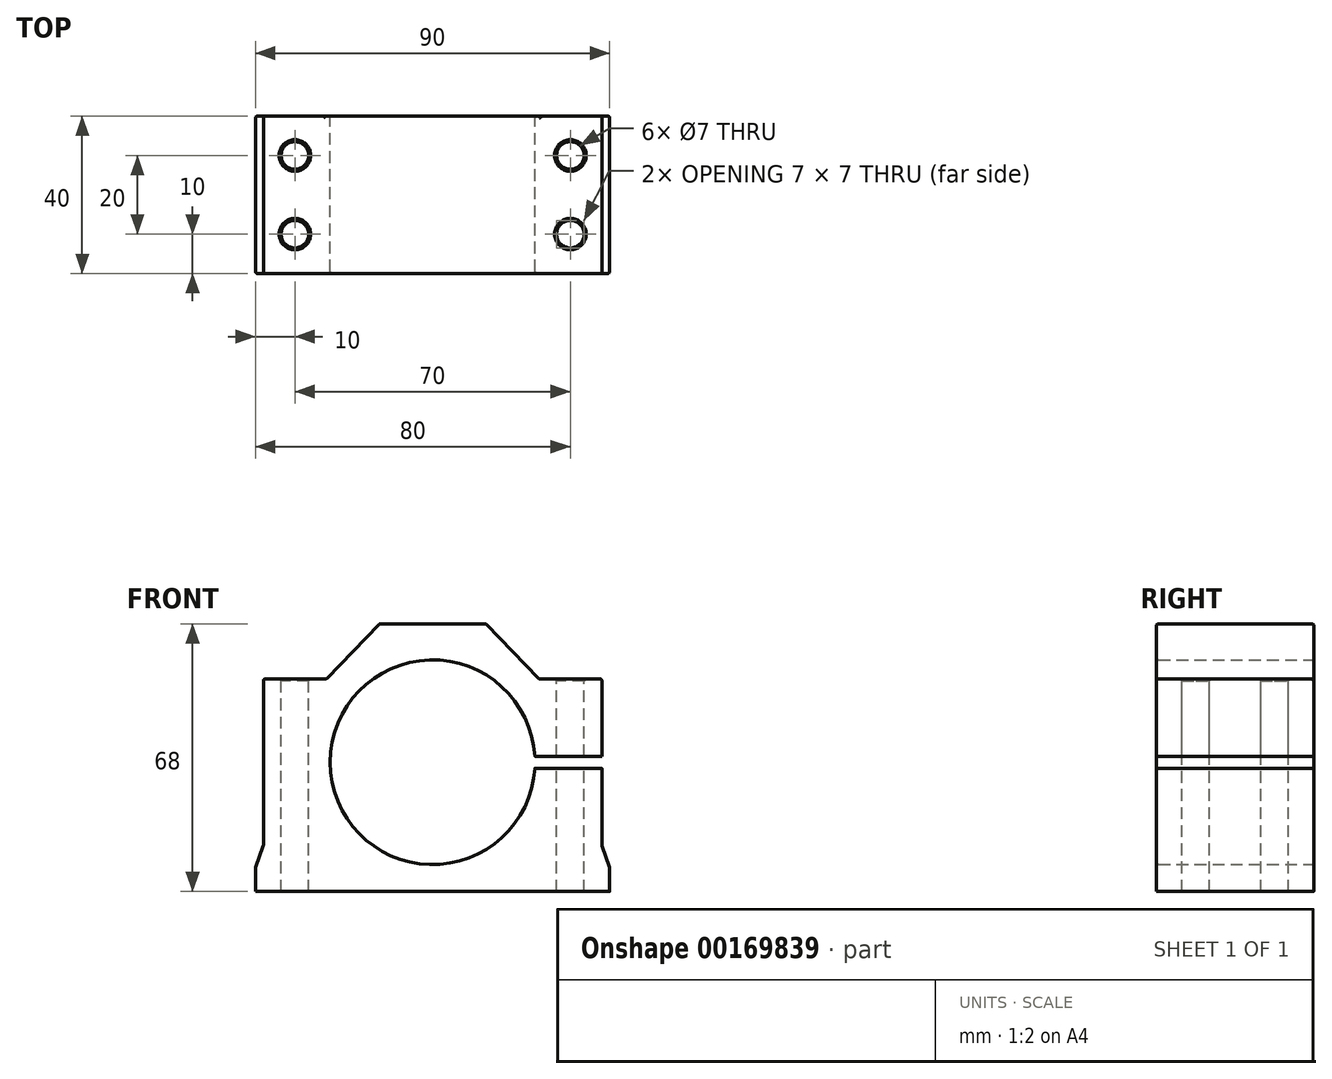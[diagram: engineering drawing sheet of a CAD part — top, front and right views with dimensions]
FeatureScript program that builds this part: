
annotation { "Feature Type Name" : "Feature", "Feature Type Description" : "" }
export const myFeature = defineFeature(function(context is Context, id is Id, definition is map)
    precondition{}
    {
        {
            var Q0;
            Q0=qCreatedBy(makeId("Front.planeOp"),FACE);
            var sketch = newSketch(context, id + "F0", { "sketchPlane" : qUnion([Q0])});
            skLineSegment(sketch, "E0", {"start": v(0, 0) * mm, "end": v(0, 68) * mm, "construction": true});
            skLineSegment(sketch, "E1", {"start": v(0, 68) * mm, "end": v(13.5, 68) * mm});
            skLineSegment(sketch, "E2", {"start": v(13.5, 68) * mm, "end": v(27, 54) * mm});
            skLineSegment(sketch, "E3", {"start": v(27, 54) * mm, "end": v(43, 54) * mm});
            skLineSegment(sketch, "E4", {"start": v(43, 54) * mm, "end": v(43, 34.32) * mm});
            skLineSegment(sketch, "E5", {"start": v(43, 11.64) * mm, "end": v(45, 6.02) * mm});
            skLineSegment(sketch, "E6", {"start": v(45, 6.02) * mm, "end": v(45, 0) * mm});
            skLineSegment(sketch, "E7", {"start": v(45, 0) * mm, "end": v(0, 0) * mm});
            skArc(sketch, "E8", {"start": v(25.96, 34.32) * mm, "mid": v(-26, 32.82) * mm, "end": v(25.96, 31.32) * mm});
            skPoint(sketch, "E8.centerSnap0", {"position": v(43, 32.82) * mm});
            skLineSegment(sketch, "E9.MirrorCS", {"start": v(0, 68) * mm, "end": v(-13.5, 68) * mm});
            skLineSegment(sketch, "E10.MirrorCS", {"start": v(-13.5, 68) * mm, "end": v(-27, 54) * mm});
            skLineSegment(sketch, "E11.MirrorCS", {"start": v(-27, 54) * mm, "end": v(-43, 54) * mm});
            skLineSegment(sketch, "E12.MirrorCS", {"start": v(-43, 54) * mm, "end": v(-43, 11.64) * mm});
            skLineSegment(sketch, "E13.MirrorCS", {"start": v(-43, 11.64) * mm, "end": v(-45, 6.02) * mm});
            skLineSegment(sketch, "E14.MirrorCS", {"start": v(-45, 6.02) * mm, "end": v(-45, 0) * mm});
            skLineSegment(sketch, "E15.MirrorCS", {"start": v(-45, 0) * mm, "end": v(0, 0) * mm});
            skLineSegment(sketch, "E16", {"start": v(43, 34.32) * mm, "end": v(25.96, 34.32) * mm});
            skLineSegment(sketch, "E17", {"start": v(43, 32.82) * mm, "end": v(0, 32.82) * mm, "construction": true});
            skLineSegment(sketch, "E18.MirrorCS", {"start": v(43, 31.32) * mm, "end": v(25.96, 31.32) * mm});
            skLineSegment(sketch, "E19.trimOffspring", {"start": v(43, 31.32) * mm, "end": v(43, 11.64) * mm});
            skSolve(sketch);
        }
        {
            var Q0;
            Q0 = qSketchRegion(id + "F0", true);
            extrude(context, id + "F1", {"entities" : qUnion([Q0]), "depth" : 40 * mm, "symmetric" : true});
        }
        {
            var Q0;
            Q0=makeQuery(id+"F1.opExtrude","SWEPT_FACE",FACE,{"disambiguationData":[OSD([sQuery(id+"F0.wireOp",EDGE,"E11.MirrorCS")])]});
            var sketch = newSketch(context, id + "F2", { "sketchPlane" : qUnion([Q0])});
            skPoint(sketch, "E20.centerSnap0", {"position": v(-35, 20) * mm});
            skPoint(sketch, "E21.centerSnap0", {"position": v(-35, -20) * mm});
            skPoint(sketch, "E22", {"position": v(-35, 10) * mm});
            skPoint(sketch, "E23", {"position": v(-35, -10) * mm});
            skLineSegment(sketch, "E24", {"start": v(0, -20) * mm, "end": v(0, 22.87) * mm, "construction": true});
            skPoint(sketch, "E25.MirrorP", {"position": v(35, 10) * mm});
            skPoint(sketch, "E26.MirrorP", {"position": v(35, -10) * mm});
            skSolve(sketch);
        }
        {
            var Q0;
            Q0=sQuery(id+"F2.wireOp",VERTEX,"E22");
            var Q1;
            Q1=sQuery(id+"F2.wireOp",VERTEX,"E23");
            var Q2;
            Q2=sQuery(id+"F2.wireOp",VERTEX,"E25.MirrorP");
            var Q3;
            Q3=sQuery(id+"F2.wireOp",VERTEX,"E26.MirrorP");
            var Q4;
            Q4=makeQuery(id+"F1.opExtrude","SWEPT_BODY",BODY,{"disambiguationData":[OSD([sQuery(id+"F0.wireOp",EDGE,"E1"),sQuery(id+"F0.wireOp",EDGE,"E2"),sQuery(id+"F0.wireOp",EDGE,"E3"),sQuery(id+"F0.wireOp",EDGE,"E4"),sQuery(id+"F0.wireOp",EDGE,"E5"),sQuery(id+"F0.wireOp",EDGE,"E6"),sQuery(id+"F0.wireOp",EDGE,"E7"),sQuery(id+"F0.wireOp",EDGE,"E8"),sQuery(id+"F0.wireOp",EDGE,"E9.MirrorCS"),sQuery(id+"F0.wireOp",EDGE,"E10.MirrorCS"),sQuery(id+"F0.wireOp",EDGE,"E11.MirrorCS"),sQuery(id+"F0.wireOp",EDGE,"E12.MirrorCS"),sQuery(id+"F0.wireOp",EDGE,"E13.MirrorCS"),sQuery(id+"F0.wireOp",EDGE,"E14.MirrorCS"),sQuery(id+"F0.wireOp",EDGE,"E15.MirrorCS"),sQuery(id+"F0.wireOp",EDGE,"E16"),sQuery(id+"F0.wireOp",EDGE,"E18.MirrorCS"),sQuery(id+"F0.wireOp",EDGE,"E19.trimOffspring")])]});
            hole(context, id + "F3", {"style" : HoleStyle.C_SINK, "endStyle" : HoleEndStyle.THROUGH, "holeDiameter" : 7 * mm, "cSinkDiameter" : 8 * mm, "cSinkAngle" : 90 * degree, "locations" : qUnion([Q0, Q1, Q2, Q3]), "scope" : qUnion([Q4]), "isTappedThrough" : true});
        }
        {
            var Q0;
            Q0=makeQuery(id+"F1.opExtrude","CAP_EDGE",EDGE,{"disambiguationData":[OSD([sQuery(id+"F0.wireOp",EDGE,"E1"),sQuery(id+"F0.wireOp",EDGE,"E9.MirrorCS")])],"isStart":false});
            var Q1;
            Q1=makeQuery(id+"F1.opExtrude","CAP_EDGE",EDGE,{"disambiguationData":[OSD([sQuery(id+"F0.wireOp",EDGE,"E10.MirrorCS")])],"isStart":false});
            var Q2;
            Q2=makeQuery(id+"F1.opExtrude","CAP_EDGE",EDGE,{"disambiguationData":[OSD([sQuery(id+"F0.wireOp",EDGE,"E2")])],"isStart":false});
            var Q3;
            Q3=makeQuery(id+"F1.opExtrude","CAP_EDGE",EDGE,{"disambiguationData":[OSD([sQuery(id+"F0.wireOp",EDGE,"E11.MirrorCS")])],"isStart":false});
            var Q4;
            Q4=makeQuery(id+"F1.opExtrude","CAP_EDGE",EDGE,{"disambiguationData":[OSD([sQuery(id+"F0.wireOp",EDGE,"E3")])],"isStart":false});
            var Q5;
            Q5=makeQuery(id+"F1.opExtrude","CAP_EDGE",EDGE,{"disambiguationData":[OSD([sQuery(id+"F0.wireOp",EDGE,"E4")])],"isStart":false});
            var Q6;
            Q6=makeQuery(id+"F1.opExtrude","CAP_EDGE",EDGE,{"disambiguationData":[OSD([sQuery(id+"F0.wireOp",EDGE,"E12.MirrorCS")])],"isStart":false});
            var Q7;
            Q7=makeQuery(id+"F1.opExtrude","CAP_EDGE",EDGE,{"disambiguationData":[OSD([sQuery(id+"F0.wireOp",EDGE,"E13.MirrorCS")])],"isStart":false});
            var Q8;
            Q8=makeQuery(id+"F1.opExtrude","CAP_EDGE",EDGE,{"disambiguationData":[OSD([sQuery(id+"F0.wireOp",EDGE,"E14.MirrorCS")])],"isStart":false});
            var Q9;
            Q9=makeQuery(id+"F1.opExtrude","CAP_EDGE",EDGE,{"disambiguationData":[OSD([sQuery(id+"F0.wireOp",EDGE,"E19.trimOffspring")])],"isStart":false});
            var Q10;
            Q10=makeQuery(id+"F1.opExtrude","CAP_EDGE",EDGE,{"disambiguationData":[OSD([sQuery(id+"F0.wireOp",EDGE,"E5")])],"isStart":false});
            var Q11;
            Q11=makeQuery(id+"F1.opExtrude","CAP_EDGE",EDGE,{"disambiguationData":[OSD([sQuery(id+"F0.wireOp",EDGE,"E6")])],"isStart":false});
            var Q12;
            Q12=makeQuery(id+"F1.opExtrude","CAP_EDGE",EDGE,{"disambiguationData":[OSD([sQuery(id+"F0.wireOp",EDGE,"E8")])],"isStart":false});
            var Q13;
            Q13=makeQuery(id+"F1.opExtrude","SWEPT_EDGE",EDGE,{"disambiguationData":[OSD([sQuery(id+"F0.wireOp",EDGE,"E11.MirrorCS"),sQuery(id+"F0.wireOp",EDGE,"E12.MirrorCS")])]});
            var Q14;
            Q14=makeQuery(id+"F1.opExtrude","SWEPT_EDGE",EDGE,{"disambiguationData":[OSD([sQuery(id+"F0.wireOp",EDGE,"E10.MirrorCS"),sQuery(id+"F0.wireOp",EDGE,"E11.MirrorCS")])]});
            var Q15;
            Q15=makeQuery(id+"F1.opExtrude","SWEPT_EDGE",EDGE,{"disambiguationData":[OSD([sQuery(id+"F0.wireOp",EDGE,"E9.MirrorCS"),sQuery(id+"F0.wireOp",EDGE,"E10.MirrorCS")])]});
            var Q16;
            Q16=makeQuery(id+"F1.opExtrude","SWEPT_EDGE",EDGE,{"disambiguationData":[OSD([sQuery(id+"F0.wireOp",EDGE,"E1"),sQuery(id+"F0.wireOp",EDGE,"E2")])]});
            var Q17;
            Q17=makeQuery(id+"F1.opExtrude","SWEPT_EDGE",EDGE,{"disambiguationData":[OSD([sQuery(id+"F0.wireOp",EDGE,"E2"),sQuery(id+"F0.wireOp",EDGE,"E3")])]});
            var Q18;
            Q18=makeQuery(id+"F1.opExtrude","CAP_EDGE",EDGE,{"disambiguationData":[OSD([sQuery(id+"F0.wireOp",EDGE,"E1"),sQuery(id+"F0.wireOp",EDGE,"E9.MirrorCS")])],"isStart":true});
            var Q19;
            Q19=makeQuery(id+"F1.opExtrude","CAP_EDGE",EDGE,{"disambiguationData":[OSD([sQuery(id+"F0.wireOp",EDGE,"E2")])],"isStart":true});
            var Q20;
            Q20=makeQuery(id+"F1.opExtrude","CAP_EDGE",EDGE,{"disambiguationData":[OSD([sQuery(id+"F0.wireOp",EDGE,"E10.MirrorCS")])],"isStart":true});
            var Q21;
            Q21=makeQuery(id+"F1.opExtrude","CAP_EDGE",EDGE,{"disambiguationData":[OSD([sQuery(id+"F0.wireOp",EDGE,"E4")])],"isStart":true});
            var Q22;
            Q22=makeQuery(id+"F1.opExtrude","CAP_EDGE",EDGE,{"disambiguationData":[OSD([sQuery(id+"F0.wireOp",EDGE,"E19.trimOffspring")])],"isStart":true});
            var Q23;
            Q23=makeQuery(id+"F1.opExtrude","CAP_EDGE",EDGE,{"disambiguationData":[OSD([sQuery(id+"F0.wireOp",EDGE,"E5")])],"isStart":true});
            var Q24;
            Q24=makeQuery(id+"F1.opExtrude","CAP_EDGE",EDGE,{"disambiguationData":[OSD([sQuery(id+"F0.wireOp",EDGE,"E6")])],"isStart":true});
            var Q25;
            Q25=makeQuery(id+"F1.opExtrude","SWEPT_EDGE",EDGE,{"disambiguationData":[OSD([sQuery(id+"F0.wireOp",EDGE,"E5"),sQuery(id+"F0.wireOp",EDGE,"E6")])]});
            var Q26;
            Q26=makeQuery(id+"F1.opExtrude","SWEPT_EDGE",EDGE,{"disambiguationData":[OSD([sQuery(id+"F0.wireOp",EDGE,"E5"),sQuery(id+"F0.wireOp",EDGE,"E19.trimOffspring")])]});
            var Q27;
            Q27=makeQuery(id+"F1.opExtrude","CAP_EDGE",EDGE,{"disambiguationData":[OSD([sQuery(id+"F0.wireOp",EDGE,"E8")])],"isStart":true});
            var Q28;
            Q28=makeQuery(id+"F1.opExtrude","CAP_EDGE",EDGE,{"disambiguationData":[OSD([sQuery(id+"F0.wireOp",EDGE,"E12.MirrorCS")])],"isStart":true});
            var Q29;
            Q29=makeQuery(id+"F1.opExtrude","CAP_EDGE",EDGE,{"disambiguationData":[OSD([sQuery(id+"F0.wireOp",EDGE,"E13.MirrorCS")])],"isStart":true});
            var Q30;
            Q30=makeQuery(id+"F1.opExtrude","CAP_EDGE",EDGE,{"disambiguationData":[OSD([sQuery(id+"F0.wireOp",EDGE,"E14.MirrorCS")])],"isStart":true});
            var Q31;
            Q31=makeQuery(id+"F1.opExtrude","SWEPT_EDGE",EDGE,{"disambiguationData":[OSD([sQuery(id+"F0.wireOp",EDGE,"E13.MirrorCS"),sQuery(id+"F0.wireOp",EDGE,"E14.MirrorCS")])]});
            var Q32;
            Q32=makeQuery(id+"F1.opExtrude","SWEPT_EDGE",EDGE,{"disambiguationData":[OSD([sQuery(id+"F0.wireOp",EDGE,"E12.MirrorCS"),sQuery(id+"F0.wireOp",EDGE,"E13.MirrorCS")])]});
            var Q33;
            Q33=makeQuery(id+"F1.opExtrude","SWEPT_EDGE",EDGE,{"disambiguationData":[OSD([sQuery(id+"F0.wireOp",EDGE,"E3"),sQuery(id+"F0.wireOp",EDGE,"E4")])]});
            fillet(context, id + "F4", {"entities" : qUnion([Q0, Q1, Q2, Q3, Q4, Q5, Q6, Q7, Q8, Q9, Q10, Q11, Q12, Q13, Q14, Q15, Q16, Q17, Q18, Q19, Q20, Q21, Q22, Q23, Q24, Q25, Q26, Q27, Q28, Q29, Q30, Q31, Q32, Q33]), "radius" : 0.5 * mm, "tangentPropagation" : true, "defaultsChanged" : true, "vertexSettings" : [], "allowEdgeOverflow" : false});
        }
    });
